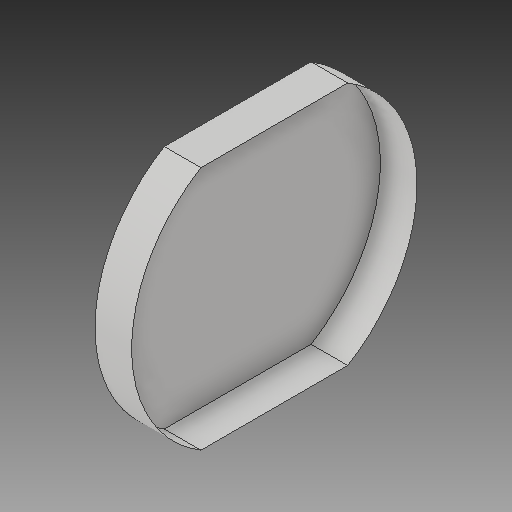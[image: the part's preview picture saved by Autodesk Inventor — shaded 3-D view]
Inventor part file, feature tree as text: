
AUTODESK INVENTOR PART (.ipt)
format: ipt  version: 2017 (Build 210142000, 142)  size: 117,760 bytes
history: native  units: in
note: dims shown in document units (in); Inventor stores cm internally (conversion verified against a paired STEP export)
features: extrude x1, delete_face x1, sketch x1
ambient origin geometry x8: Origin, YZ Plane, XZ Plane, XY Plane, X Axis, Y Axis, Z Axis, Center Point
bodies: Solid2 (feature_tree)
feature tree (3):
  extrude  "connection"  [1 undecoded]
  delete_face  "Delete Face1"
  sketch  "Sketch1"  dims[d12=6.6667in d14=1.0in d15=0.0in d85=4.0in d87=3.8873in d88=3.8873in d92=1.6458in d98=3.3333in]
note: 1 required parameter value undecoded (feature->parameter linkage not recoverable at this tier; creation-order binding heuristic only, values carry confidence <= 0.55)
